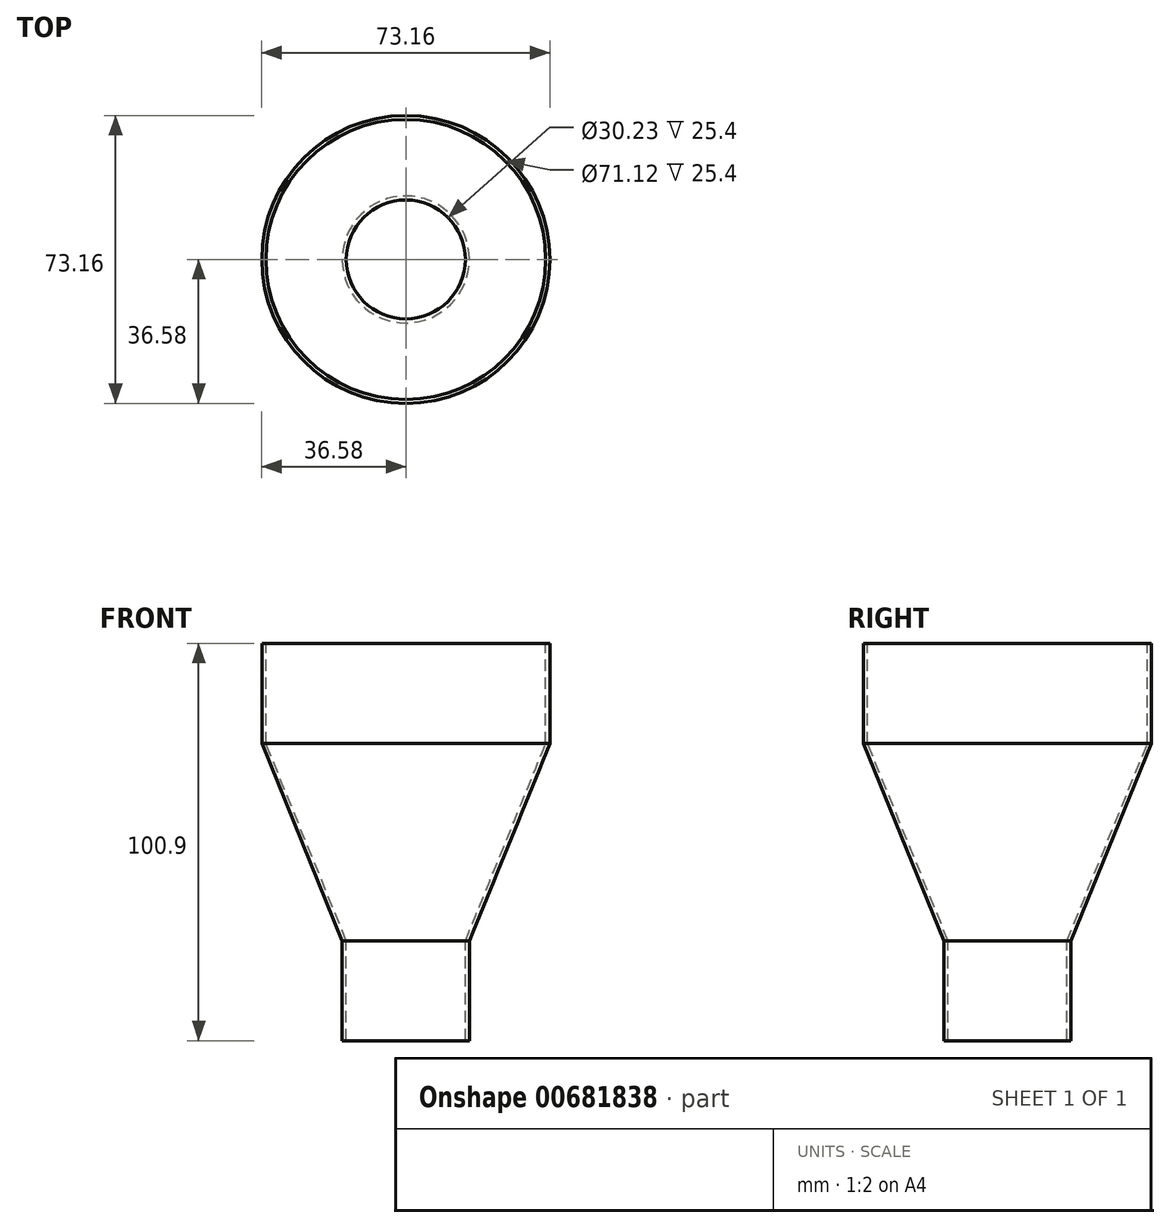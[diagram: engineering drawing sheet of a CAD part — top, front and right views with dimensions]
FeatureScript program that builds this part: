
annotation { "Feature Type Name" : "Feature", "Feature Type Description" : "" }
export const myFeature = defineFeature(function(context is Context, id is Id, definition is map)
    precondition{}
    {
        {
            var Q0;
            Q0=qCreatedBy(makeId("Front.planeOp"),FACE);
            var sketch = newSketch(context, id + "F0", { "sketchPlane" : qUnion([Q0])});
            skLineSegment(sketch, "E0", {"start": v(-35.56, 0) * mm, "end": v(-15.11, -50.1) * mm});
            skLineSegment(sketch, "E1", {"start": v(-15.11, -50.1) * mm, "end": v(-15.11, -75.5) * mm});
            skLineSegment(sketch, "E2", {"start": v(0, 0) * mm, "end": v(0, -75.5) * mm});
            skLineSegment(sketch, "E3", {"start": v(-35.56, 0) * mm, "end": v(-35.56, 25.4) * mm});
            skLineSegment(sketch, "E4", {"start": v(-35.56, 25.4) * mm, "end": v(-36.58, 25.4) * mm});
            skLineSegment(sketch, "E5", {"start": v(-36.58, 25.4) * mm, "end": v(-36.58, 0) * mm});
            skLineSegment(sketch, "E6", {"start": v(-36.58, 0) * mm, "end": v(-16.13, -50.1) * mm});
            skLineSegment(sketch, "E7", {"start": v(-16.13, -50.1) * mm, "end": v(-15.11, -50.1) * mm});
            skLineSegment(sketch, "E8", {"start": v(-16.13, -50.1) * mm, "end": v(-16.13, -75.5) * mm});
            skLineSegment(sketch, "E9", {"start": v(-16.13, -75.5) * mm, "end": v(-15.11, -75.5) * mm});
            skLineSegment(sketch, "E10", {"start": v(-36.58, 0) * mm, "end": v(-35.56, 0) * mm});
            skLineSegment(sketch, "E11", {"start": v(-15.11, -75.5) * mm, "end": v(0, -75.5) * mm});
            skLineSegment(sketch, "E12", {"start": v(0, 1.31) * mm, "end": v(0, 22.7) * mm});
            skLineSegment(sketch, "E13", {"start": v(-35.56, 25.4) * mm, "end": v(0, 25.4) * mm});
            skSolve(sketch);
        }
        {
            var Q0;
            Q0=makeQuery(id+"F0.imprint","IMPRINT",FACE,{"disambiguationData":[TD([[makeQuery(id+"F0.imprint","IMPRINT",EDGE,{"derivedFrom":sQuery(id+"F0.wireOp",EDGE,"E1")}),-1.0]])]});
            var Q1;
            Q1=makeQuery(id+"F0.imprint","IMPRINT",FACE,{"disambiguationData":[TD([[makeQuery(id+"F0.imprint","IMPRINT",EDGE,{"derivedFrom":sQuery(id+"F0.wireOp",EDGE,"E0")}),-1.0]])]});
            var Q2;
            Q2=makeQuery(id+"F0.imprint","IMPRINT",FACE,{"disambiguationData":[TD([[makeQuery(id+"F0.imprint","IMPRINT",EDGE,{"derivedFrom":sQuery(id+"F0.wireOp",EDGE,"E3")}),1.0]])]});
            var Q3;
            Q3=sQuery(id+"F0.wireOp",EDGE,"E5");
            var Q4;
            Q4=sQuery(id+"F0.wireOp",EDGE,"E4");
            var Q5;
            Q5=sQuery(id+"F0.wireOp",EDGE,"E3");
            var Q6;
            Q6=sQuery(id+"F0.wireOp",EDGE,"E6");
            var Q7;
            Q7=sQuery(id+"F0.wireOp",EDGE,"E0");
            var Q8;
            Q8=sQuery(id+"F0.wireOp",EDGE,"E2");
            revolve(context, id + "F1", {"entities" : qUnion([Q0, Q1, Q2]), "surfaceEntities" : qUnion([Q3, Q4, Q5, Q6, Q7]), "axis" : qUnion([Q8]), "revolveType" : RevolveType.FULL});
        }
    });
